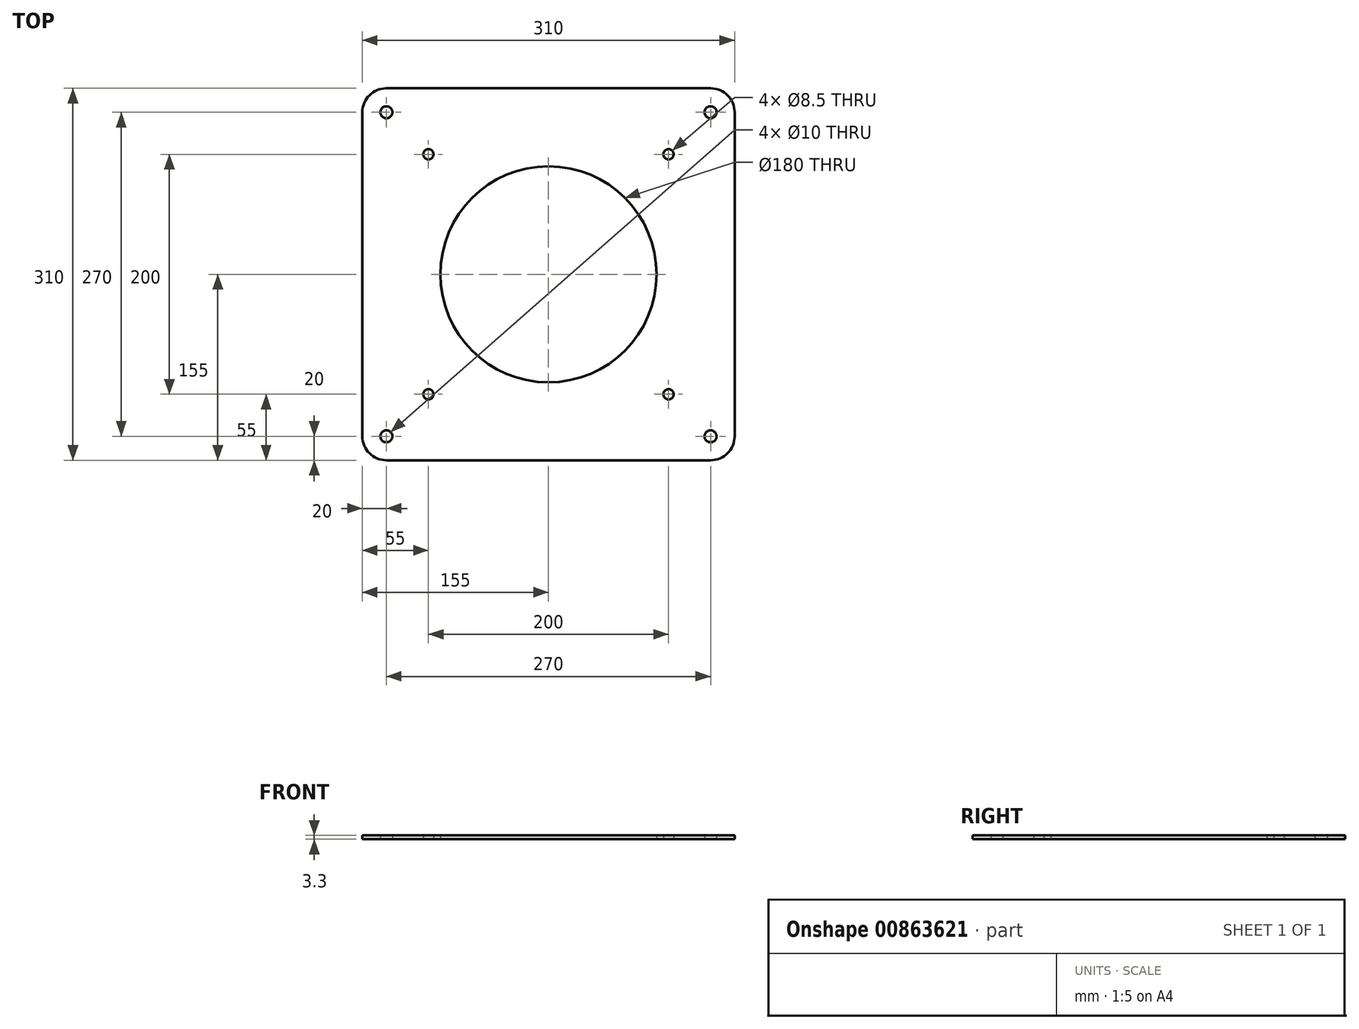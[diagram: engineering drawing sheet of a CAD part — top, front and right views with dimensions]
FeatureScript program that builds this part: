
annotation { "Feature Type Name" : "Feature", "Feature Type Description" : "" }
export const myFeature = defineFeature(function(context is Context, id is Id, definition is map)
    precondition{}
    {
        {
            var Q0;
            Q0=qCreatedBy(makeId("Top.planeOp"),FACE);
            var sketch = newSketch(context, id + "F0", { "sketchPlane" : qUnion([Q0])});
            skCircle(sketch, "E0", {"center": v(0, 0) * mm, "radius": 4.25 * mm});
            skCircle(sketch, "E1", {"center": v(-35, -35) * mm, "radius": 5 * mm});
            skCircle(sketch, "E2.0.1.0", {"center": v(0, 200) * mm, "radius": 4.25 * mm});
            skCircle(sketch, "E2.1.0.0", {"center": v(200, 0) * mm, "radius": 4.25 * mm});
            skCircle(sketch, "E2.1.1.0", {"center": v(200, 200) * mm, "radius": 4.25 * mm});
            skLineSegment(sketch, "E2.direction1", {"start": v(0, 0) * mm, "end": v(200, 0) * mm, "construction": true});
            skLineSegment(sketch, "E2.direction2", {"start": v(0, 0) * mm, "end": v(0, 200) * mm, "construction": true});
            skCircle(sketch, "E3.0.1.0", {"center": v(-35, 235) * mm, "radius": 5 * mm});
            skCircle(sketch, "E3.1.0.0", {"center": v(235, -35) * mm, "radius": 5 * mm});
            skCircle(sketch, "E3.1.1.0", {"center": v(235, 235) * mm, "radius": 5 * mm});
            skLineSegment(sketch, "E3.direction1", {"start": v(-35, -35) * mm, "end": v(235, -35) * mm, "construction": true});
            skLineSegment(sketch, "E3.direction2", {"start": v(-35, -35) * mm, "end": v(-35, 235) * mm, "construction": true});
            skCircle(sketch, "E4", {"center": v(100, 100) * mm, "radius": 90 * mm});
            skLineSegment(sketch, "E5.bottom", {"start": v(-35, 255) * mm, "end": v(235, 255) * mm});
            skLineSegment(sketch, "E5.top", {"start": v(-35, -55) * mm, "end": v(235, -55) * mm});
            skLineSegment(sketch, "E5.left", {"start": v(-55, 235) * mm, "end": v(-55, -35) * mm});
            skLineSegment(sketch, "E5.right", {"start": v(255, 235) * mm, "end": v(255, -35) * mm});
            skPoint(sketch, "E6.visualSharp", {"position": v(-55, 255) * mm});
            skArc(sketch, "E6.filletArc", {"start": v(-35, 255) * mm, "mid": v(-49.14, 249.14) * mm, "end": v(-55, 235) * mm});
            skPoint(sketch, "E7.visualSharp", {"position": v(255, 255) * mm});
            skArc(sketch, "E7.filletArc", {"start": v(255, 235) * mm, "mid": v(249.14, 249.14) * mm, "end": v(235, 255) * mm});
            skPoint(sketch, "E8.visualSharp", {"position": v(255, -55) * mm});
            skArc(sketch, "E8.filletArc", {"start": v(235, -55) * mm, "mid": v(249.14, -49.14) * mm, "end": v(255, -35) * mm});
            skPoint(sketch, "E9.visualSharp", {"position": v(-55, -55) * mm});
            skArc(sketch, "E9.filletArc", {"start": v(-55, -35) * mm, "mid": v(-49.14, -49.14) * mm, "end": v(-35, -55) * mm});
            skSolve(sketch);
        }
        {
            var Q0;
            Q0=makeQuery(id+"F0.imprint","IMPRINT",FACE,{"disambiguationData":[TD([[makeQuery(id+"F0.imprint","IMPRINT",EDGE,{"derivedFrom":sQuery(id+"F0.wireOp",EDGE,"E0")}),-1.0]])]});
            extrude(context, id + "F1", {"entities" : qUnion([Q0]), "depth" : 3.3 * mm, "offsetDistance" : 25 * mm});
        }
    });
